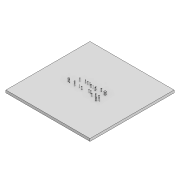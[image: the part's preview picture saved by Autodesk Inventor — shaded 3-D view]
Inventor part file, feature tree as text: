
AUTODESK INVENTOR PART (.ipt)
format: ipt  version: 2021 (Build 250183000, 183)  size: 326,144 bytes
history: native  units: in
note: dims shown in document units (in); Inventor stores cm internally (conversion verified against a paired STEP export)
features: sketch x7, extrude x6, projected_geometry x5, fillet x1
ambient origin geometry x8: Origin, YZ Plane, XZ Plane, XY Plane, X Axis, Y Axis, Z Axis, Center Point
bodies: Solid1 (feature_tree)
feature tree (19):
  extrude  "Extrusion1"  Depth=3937.0079in
  extrude  "Extrusion2"  Depth=118.1102in
  fillet  "Fillet1"  Radius=118.1102in
  extrude  "Extrusion3"  Depth=118.1102in TaperAngle=0.0deg
  extrude  "Extrusion4"  TaperAngle=0.0deg  [1 undecoded]
  sketch  "Sketch5"  dims[d14=118.1102in d15=0.0in]
  extrude  "Extrusion5"  [1 undecoded]
  extrude  "Extrusion6"  [1 undecoded]
  sketch  "Sketch1"  dims[d0=3937.0079in d1=3937.0079in]
  sketch  "Sketch2"  dims[d2=118.1102in d3=0.0in d4=157.4803in d5=118.1102in d6=0.0in]
  projected_geometry  "Projected Loop1"
  sketch  "Sketch3"  dims[d7=19.685in d8=118.1102in d9=0.0in]
  projected_geometry  "Projected Loop2"
  sketch  "Sketch4"  dims[d10=1.0in d11=0.0in d12=0.0in d13=0.0in]
  projected_geometry  "Projected Loop3"
  projected_geometry  "Projected Loop4"
  sketch  "Sketch6"
  projected_geometry  "Projected Loop5"
  sketch  "Sketch7"
note: 3 required parameter values undecoded (feature->parameter linkage not recoverable at this tier; creation-order binding heuristic only, values carry confidence <= 0.55)
